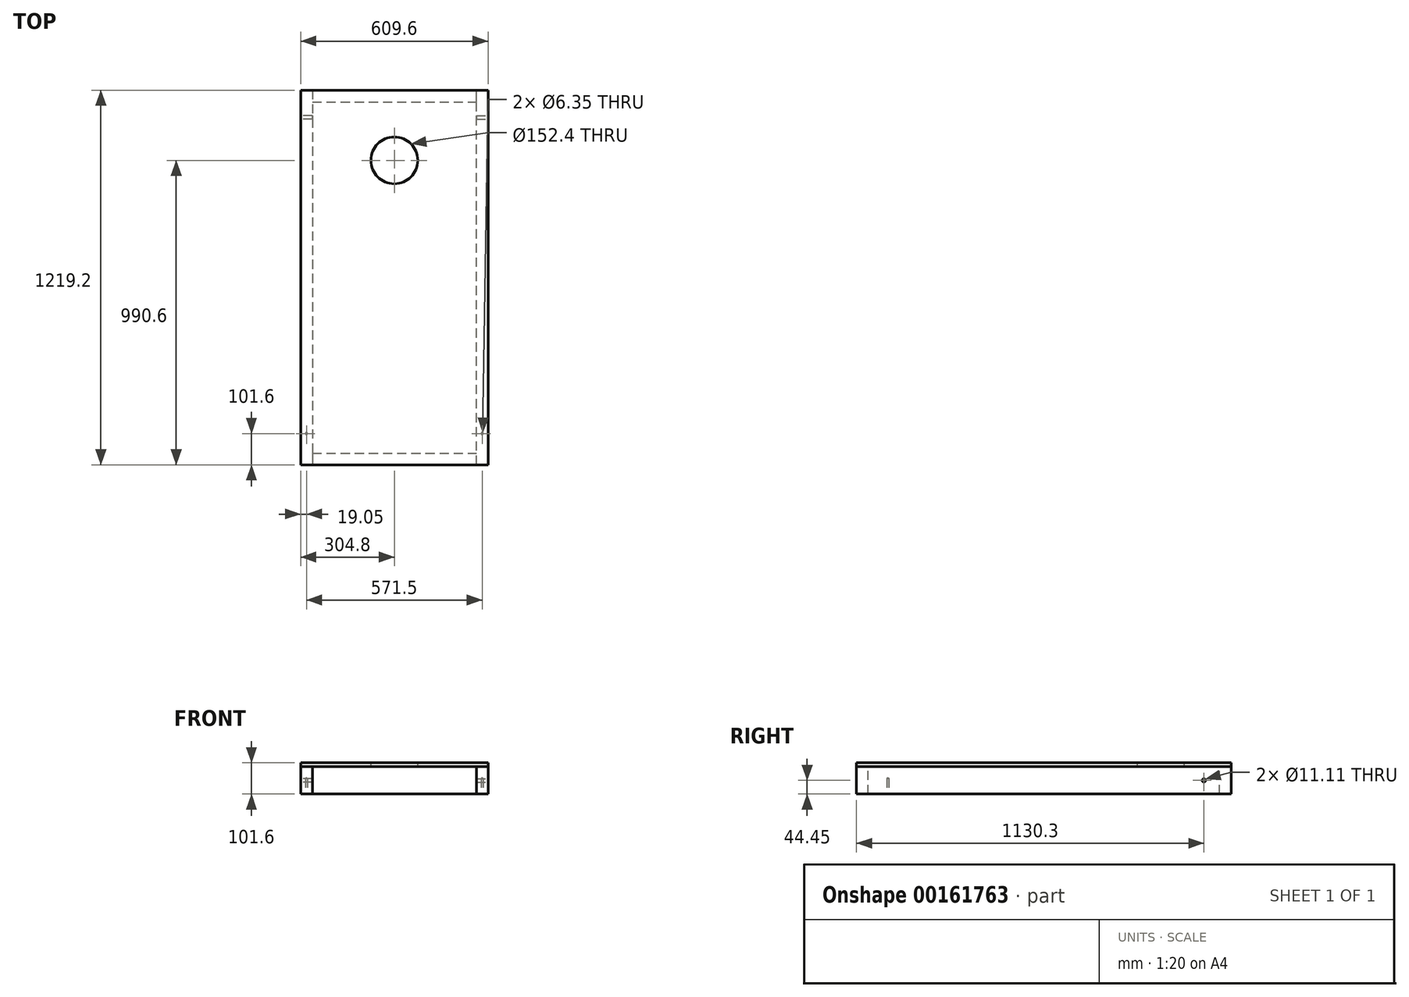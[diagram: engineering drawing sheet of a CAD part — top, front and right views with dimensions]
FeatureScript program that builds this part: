
annotation { "Feature Type Name" : "Feature", "Feature Type Description" : "" }
export const myFeature = defineFeature(function(context is Context, id is Id, definition is map)
    precondition{}
    {
        {
            var Q0;
            Q0=qCreatedBy(makeId("Top.planeOp"),FACE);
            var sketch = newSketch(context, id + "F0", { "sketchPlane" : qUnion([Q0])});
            skLineSegment(sketch, "E0.bottom", {"start": v(0, 0) * mm, "end": v(609.6, 0) * mm});
            skLineSegment(sketch, "E0.top", {"start": v(0, 1219.2) * mm, "end": v(609.6, 1219.2) * mm});
            skLineSegment(sketch, "E0.left", {"start": v(0, 0) * mm, "end": v(0, 1219.2) * mm});
            skLineSegment(sketch, "E0.right", {"start": v(609.6, 0) * mm, "end": v(609.6, 1219.2) * mm});
            skCircle(sketch, "E1", {"center": v(304.8, 990.6) * mm, "radius": 76.2 * mm});
            skSolve(sketch);
        }
        {
            var Q0;
            Q0=makeQuery(id+"F0.imprint","IMPRINT",FACE,{"disambiguationData":[TD([[makeQuery(id+"F0.imprint","IMPRINT",EDGE,{"derivedFrom":sQuery(id+"F0.wireOp",EDGE,"E0.bottom")}),1.0]])]});
            extrude(context, id + "F1", {"entities" : qUnion([Q0]), "oppositeDirection" : true, "depth" : 12.7 * mm});
        }
        {
            var Q0;
            Q0=makeQuery(id+"F1.opExtrude","CAP_FACE",FACE,{"disambiguationData":[OSD([sQuery(id+"F0.wireOp",EDGE,"E0.bottom"),sQuery(id+"F0.wireOp",EDGE,"E0.top"),sQuery(id+"F0.wireOp",EDGE,"E0.left"),sQuery(id+"F0.wireOp",EDGE,"E0.right"),sQuery(id+"F0.wireOp",EDGE,"E1")])],"isStart":false});
            var sketch = newSketch(context, id + "F2", { "sketchPlane" : qUnion([Q0])});
            skLineSegment(sketch, "E2.bottom", {"start": v(0, -1219.2) * mm, "end": v(38.1, -1219.2) * mm});
            skLineSegment(sketch, "E2.top", {"start": v(0, 0) * mm, "end": v(38.1, 0) * mm});
            skLineSegment(sketch, "E2.left", {"start": v(0, -1219.2) * mm, "end": v(0, 0) * mm});
            skLineSegment(sketch, "E2.right", {"start": v(38.1, -1219.2) * mm, "end": v(38.1, 0) * mm});
            skLineSegment(sketch, "E3.bottom", {"start": v(609.6, 0) * mm, "end": v(571.5, 0) * mm});
            skLineSegment(sketch, "E3.top", {"start": v(609.6, -1219.2) * mm, "end": v(571.5, -1219.2) * mm});
            skLineSegment(sketch, "E3.left", {"start": v(609.6, 0) * mm, "end": v(609.6, -1219.2) * mm});
            skLineSegment(sketch, "E3.right", {"start": v(571.5, 0) * mm, "end": v(571.5, -1219.2) * mm});
            skLineSegment(sketch, "E4.bottom", {"start": v(38.1, 0) * mm, "end": v(571.5, 0) * mm});
            skLineSegment(sketch, "E4.top", {"start": v(38.1, -38.1) * mm, "end": v(571.5, -38.1) * mm});
            skLineSegment(sketch, "E4.left", {"start": v(38.1, 0) * mm, "end": v(38.1, -38.1) * mm});
            skLineSegment(sketch, "E4.right", {"start": v(571.5, 0) * mm, "end": v(571.5, -38.1) * mm});
            skLineSegment(sketch, "E5.bottom", {"start": v(38.1, -1219.2) * mm, "end": v(571.5, -1219.2) * mm});
            skLineSegment(sketch, "E5.top", {"start": v(38.1, -1181.1) * mm, "end": v(571.5, -1181.1) * mm});
            skLineSegment(sketch, "E5.left", {"start": v(38.1, -1219.2) * mm, "end": v(38.1, -1181.1) * mm});
            skLineSegment(sketch, "E5.right", {"start": v(571.5, -1219.2) * mm, "end": v(571.5, -1181.1) * mm});
            skSolve(sketch);
        }
        {
            var Q0;
            Q0=makeQuery(id+"F2.imprint","IMPRINT",FACE,{"disambiguationData":[TD([[makeQuery(id+"F2.imprint","IMPRINT",EDGE,{"derivedFrom":sQuery(id+"F2.wireOp",EDGE,"E2.bottom")}),1.0]])]});
            var Q1;
            Q1=makeQuery(id+"F2.imprint","IMPRINT",FACE,{"disambiguationData":[TD([[makeQuery(id+"F2.imprint","IMPRINT",EDGE,{"derivedFrom":sQuery(id+"F2.wireOp",EDGE,"E3.bottom")}),-1.0]])]});
            extrude(context, id + "F3", {"entities" : qUnion([Q0, Q1]), "depth" : 88.9 * mm});
        }
        {
            var Q0;
            Q0=makeQuery(id+"F2.imprint","IMPRINT",FACE,{"disambiguationData":[TD([[makeQuery(id+"F2.imprint","IMPRINT",EDGE,{"derivedFrom":sQuery(id+"F2.wireOp",EDGE,"E4.bottom")}),-1.0]])]});
            var Q1;
            Q1=makeQuery(id+"F2.imprint","IMPRINT",FACE,{"disambiguationData":[TD([[makeQuery(id+"F2.imprint","IMPRINT",EDGE,{"derivedFrom":sQuery(id+"F2.wireOp",EDGE,"E5.bottom")}),1.0]])]});
            extrude(context, id + "F4", {"entities" : qUnion([Q0, Q1]), "depth" : 88.9 * mm});
        }
        {
            var Q0;
            Q0=makeQuery(id+"F3.opExtrude","SWEPT_FACE",FACE,{"disambiguationData":[OSD([sQuery(id+"F2.wireOp",EDGE,"E3.left")])]});
            var sketch = newSketch(context, id + "F5", { "sketchPlane" : qUnion([Q0])});
            skLineSegment(sketch, "E6.0.1", {"start": v(1181.1, -12.7) * mm, "end": v(1181.1, -101.6) * mm});
            skLineSegment(sketch, "E6.0.3", {"start": v(1181.1, -101.6) * mm, "end": v(1181.1, -12.7) * mm});
            skPoint(sketch, "E7", {"position": v(1130.3, -57.15) * mm});
            skSolve(sketch);
        }
        {
            var Q0;
            Q0=sQuery(id+"F5.wireOp",VERTEX,"E7");
            var Q1;
            Q1=makeQuery(id+"F3.opExtrude","SWEPT_BODY",BODY,{"disambiguationData":[OSD([sQuery(id+"F2.wireOp",EDGE,"E3.bottom"),sQuery(id+"F2.wireOp",EDGE,"E3.top"),sQuery(id+"F2.wireOp",EDGE,"E3.left"),sQuery(id+"F2.wireOp",EDGE,"E3.right"),sQuery(id+"F2.wireOp",EDGE,"E4.right"),sQuery(id+"F2.wireOp",EDGE,"E5.right")])]});
            hole(context, id + "F6", {"style" : HoleStyle.SIMPLE, "endStyle" : HoleEndStyle.THROUGH, "holeDiameter" : 11.1 * mm, "startFromSketch" : true, "locations" : qUnion([Q0]), "scope" : qUnion([Q1]), "isTappedThrough" : true});
        }
        {
            var Q0;
            Q0=makeQuery(id+"F3.opExtrude","SWEPT_FACE",FACE,{"disambiguationData":[OSD([sQuery(id+"F2.wireOp",EDGE,"E2.left")])]});
            var sketch = newSketch(context, id + "F7", { "sketchPlane" : qUnion([Q0])});
            skPoint(sketch, "E8", {"position": v(-1130.3, -57.15) * mm});
            skSolve(sketch);
        }
        {
            var Q0;
            Q0=sQuery(id+"F7.wireOp",VERTEX,"E8");
            var Q1;
            Q1=makeQuery(id+"F3.opExtrude","SWEPT_BODY",BODY,{"disambiguationData":[OSD([sQuery(id+"F2.wireOp",EDGE,"E2.bottom"),sQuery(id+"F2.wireOp",EDGE,"E2.top"),sQuery(id+"F2.wireOp",EDGE,"E2.left"),sQuery(id+"F2.wireOp",EDGE,"E2.right"),sQuery(id+"F2.wireOp",EDGE,"E4.left"),sQuery(id+"F2.wireOp",EDGE,"E5.left")])]});
            hole(context, id + "F8", {"style" : HoleStyle.SIMPLE, "endStyle" : HoleEndStyle.THROUGH, "holeDiameter" : 11.1 * mm, "startFromSketch" : true, "locations" : qUnion([Q0]), "scope" : qUnion([Q1]), "isTappedThrough" : true});
        }
        {
            var Q0;
            Q0=makeQuery(id+"F3.opExtrude","CAP_FACE",FACE,{"disambiguationData":[OSD([sQuery(id+"F2.wireOp",EDGE,"E2.bottom"),sQuery(id+"F2.wireOp",EDGE,"E2.top"),sQuery(id+"F2.wireOp",EDGE,"E2.left"),sQuery(id+"F2.wireOp",EDGE,"E2.right"),sQuery(id+"F2.wireOp",EDGE,"E4.left"),sQuery(id+"F2.wireOp",EDGE,"E5.left")])],"isStart":false});
            var sketch = newSketch(context, id + "F9", { "sketchPlane" : qUnion([Q0])});
            skPoint(sketch, "E9", {"position": v(19.05, -101.6) * mm});
            skSolve(sketch);
        }
        {
            var Q0;
            Q0=sQuery(id+"F9.wireOp",VERTEX,"E9");
            var Q1;
            Q1=makeQuery(id+"F3.opExtrude","SWEPT_BODY",BODY,{"disambiguationData":[OSD([sQuery(id+"F2.wireOp",EDGE,"E2.bottom"),sQuery(id+"F2.wireOp",EDGE,"E2.top"),sQuery(id+"F2.wireOp",EDGE,"E2.left"),sQuery(id+"F2.wireOp",EDGE,"E2.right"),sQuery(id+"F2.wireOp",EDGE,"E4.left"),sQuery(id+"F2.wireOp",EDGE,"E5.left")])]});
            hole(context, id + "F10", {"style" : HoleStyle.SIMPLE, "endStyle" : HoleEndStyle.BLIND, "holeDiameter" : 6.35 * mm, "holeDepth" : 50.8 * mm, "startFromSketch" : true, "locations" : qUnion([Q0]), "scope" : qUnion([Q1])});
        }
        {
            var Q0;
            Q0=makeQuery(id+"F3.opExtrude","CAP_FACE",FACE,{"disambiguationData":[OSD([sQuery(id+"F2.wireOp",EDGE,"E3.bottom"),sQuery(id+"F2.wireOp",EDGE,"E3.top"),sQuery(id+"F2.wireOp",EDGE,"E3.left"),sQuery(id+"F2.wireOp",EDGE,"E3.right"),sQuery(id+"F2.wireOp",EDGE,"E4.right"),sQuery(id+"F2.wireOp",EDGE,"E5.right")])],"isStart":false});
            var sketch = newSketch(context, id + "F11", { "sketchPlane" : qUnion([Q0])});
            skPoint(sketch, "E10", {"position": v(590.55, -101.6) * mm});
            skSolve(sketch);
        }
        {
            var Q0;
            Q0=sQuery(id+"F11.wireOp",VERTEX,"E10");
            var Q1;
            Q1=makeQuery(id+"F3.opExtrude","SWEPT_BODY",BODY,{"disambiguationData":[OSD([sQuery(id+"F2.wireOp",EDGE,"E3.bottom"),sQuery(id+"F2.wireOp",EDGE,"E3.top"),sQuery(id+"F2.wireOp",EDGE,"E3.left"),sQuery(id+"F2.wireOp",EDGE,"E3.right"),sQuery(id+"F2.wireOp",EDGE,"E4.right"),sQuery(id+"F2.wireOp",EDGE,"E5.right")])]});
            hole(context, id + "F12", {"style" : HoleStyle.SIMPLE, "endStyle" : HoleEndStyle.BLIND, "holeDiameter" : 6.35 * mm, "holeDepth" : 50.8 * mm, "startFromSketch" : true, "locations" : qUnion([Q0]), "scope" : qUnion([Q1])});
        }
    });
